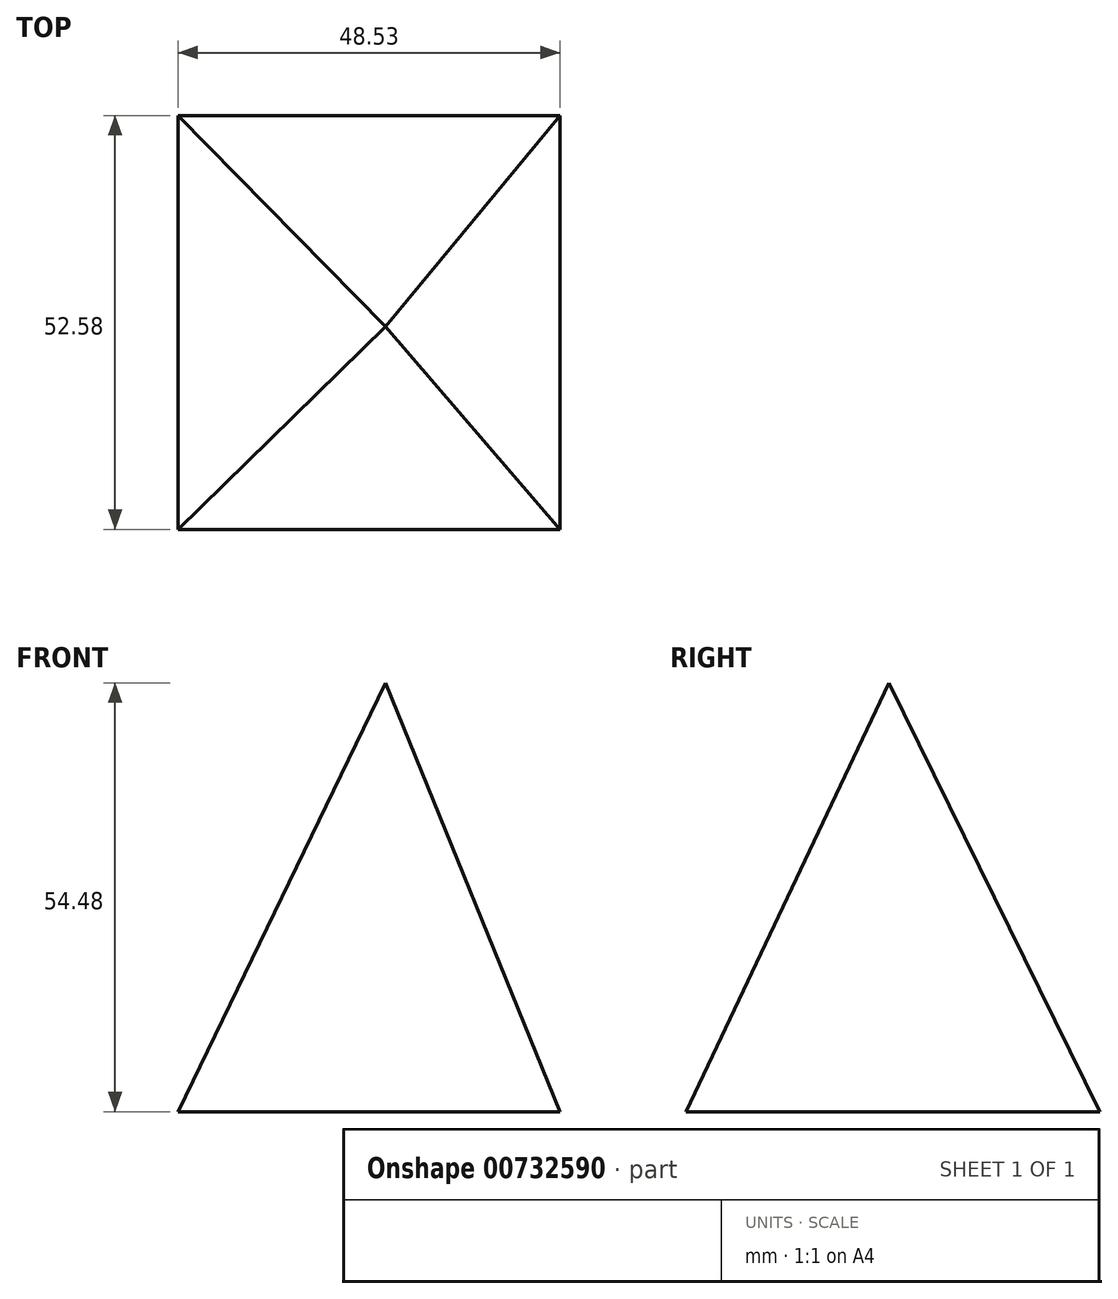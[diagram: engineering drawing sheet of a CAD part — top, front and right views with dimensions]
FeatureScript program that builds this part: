
annotation { "Feature Type Name" : "Feature", "Feature Type Description" : "" }
export const myFeature = defineFeature(function(context is Context, id is Id, definition is map)
    precondition{}
    {
        {
            var Q0;
            Q0=qCreatedBy(makeId("Front.planeOp"),FACE);
            var sketch = newSketch(context, id + "F0", { "sketchPlane" : qUnion([Q0])});
            skLineSegment(sketch, "E0", {"start": v(-90.27, -22.56) * mm, "end": v(-63.95, 31.92) * mm});
            skLineSegment(sketch, "E1", {"start": v(-63.95, 31.92) * mm, "end": v(-41.74, -22.56) * mm});
            skLineSegment(sketch, "E2", {"start": v(-41.74, -22.56) * mm, "end": v(-90.27, -22.56) * mm});
            skSolve(sketch);
        }
        {
            var Q0;
            Q0=makeQuery(id+"F0.imprint","IMPRINT",FACE,{"disambiguationData":[TD([[makeQuery(id+"F0.imprint","IMPRINT",EDGE,{"derivedFrom":sQuery(id+"F0.wireOp",EDGE,"E0")}),-1.0]])]});
            extrude(context, id + "F1", {"entities" : qUnion([Q0]), "depth" : 52.58 * mm, "offsetDistance" : 25.4 * mm});
        }
        {
            var Q0;
            Q0=qCreatedBy(makeId("Right.planeOp"),FACE);
            var sketch = newSketch(context, id + "F2", { "sketchPlane" : qUnion([Q0])});
            skLineSegment(sketch, "E3", {"start": v(-52.58, -22.56) * mm, "end": v(-26.83, 31.92) * mm});
            skLineSegment(sketch, "E4", {"start": v(-26.83, 31.92) * mm, "end": v(0, -22.56) * mm});
            skLineSegment(sketch, "E5", {"start": v(0, -22.56) * mm, "end": v(-52.58, -22.56) * mm});
            skSolve(sketch);
        }
        {
            var Q0;
            Q0=makeQuery(id+"F2.imprint","IMPRINT",FACE,{"disambiguationData":[TD([[makeQuery(id+"F2.imprint","IMPRINT",EDGE,{"derivedFrom":sQuery(id+"F2.wireOp",EDGE,"E3")}),-1.0]])]});
            extrude(context, id + "F3", {"entities" : qUnion([Q0]), "operationType" : NewBodyOperationType.INTERSECT, "oppositeDirection" : true, "depth" : 119.63 * mm, "offsetDistance" : 25.4 * mm});
        }
    });
